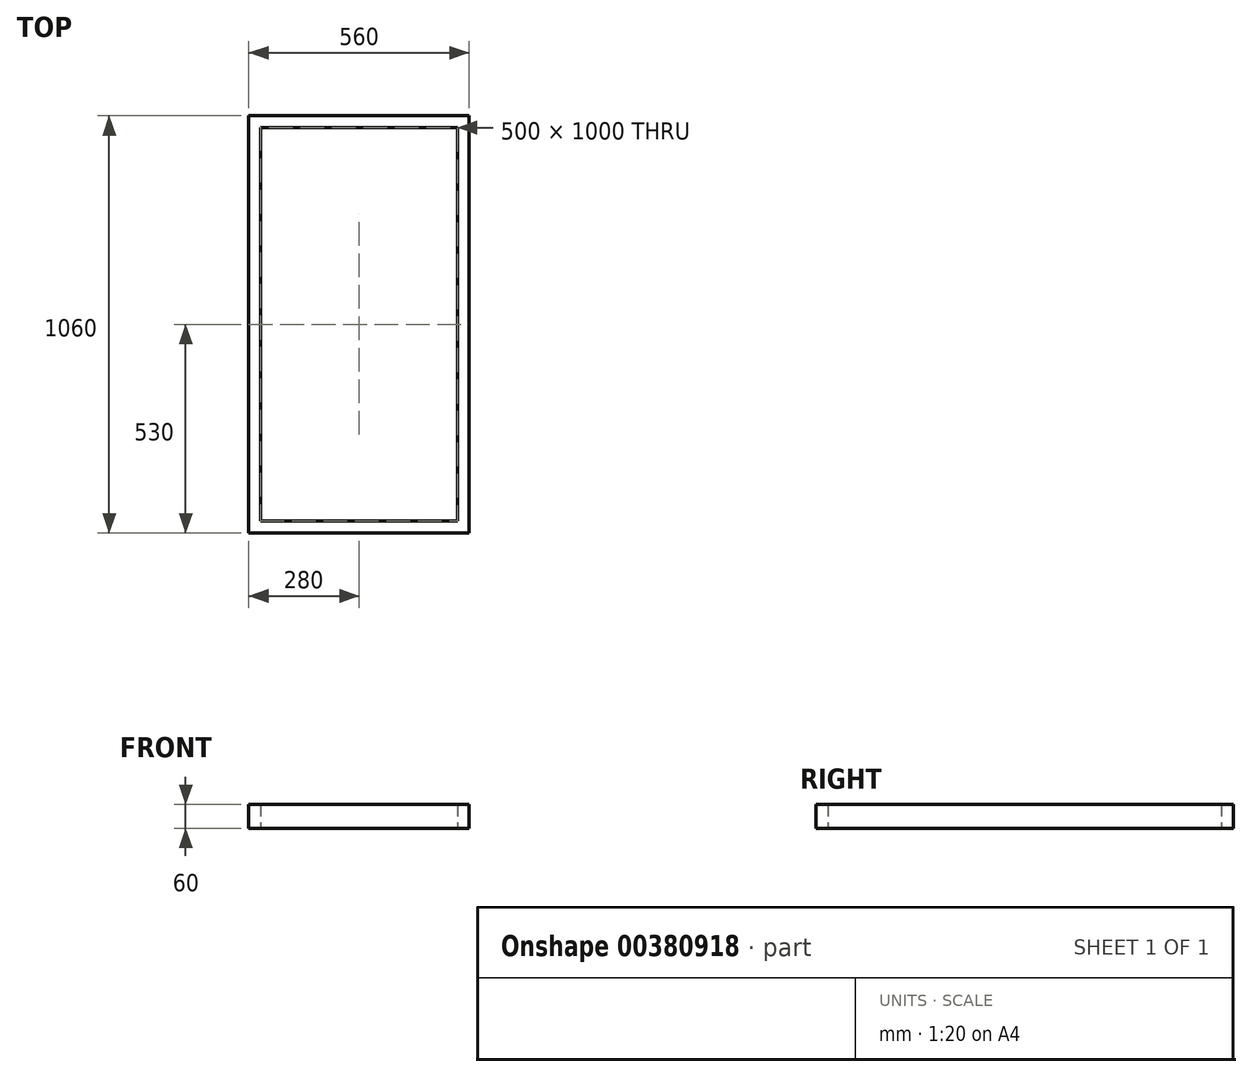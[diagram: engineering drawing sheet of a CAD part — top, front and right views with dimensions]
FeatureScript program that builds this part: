
annotation { "Feature Type Name" : "Feature", "Feature Type Description" : "" }
export const myFeature = defineFeature(function(context is Context, id is Id, definition is map)
    precondition{}
    {
        {
            var Q0;
            Q0=qCreatedBy(makeId("Top.planeOp"),FACE);
            var sketch = newSketch(context, id + "F0", { "sketchPlane" : qUnion([Q0])});
            skLineSegment(sketch, "E0.bottom", {"start": v(250, 500) * mm, "end": v(-250, 500) * mm});
            skLineSegment(sketch, "E0.top", {"start": v(250, -500) * mm, "end": v(-250, -500) * mm});
            skLineSegment(sketch, "E0.left", {"start": v(250, 500) * mm, "end": v(250, -500) * mm});
            skLineSegment(sketch, "E0.right", {"start": v(-250, 500) * mm, "end": v(-250, -500) * mm});
            skPoint(sketch, "E0.middle", {"position": v(0, 0) * mm});
            skLineSegment(sketch, "E1.0", {"start": v(-280, 530) * mm, "end": v(-280, -530) * mm});
            skLineSegment(sketch, "E1.1", {"start": v(280, 530) * mm, "end": v(-280, 530) * mm});
            skLineSegment(sketch, "E1.2", {"start": v(280, 530) * mm, "end": v(280, -530) * mm});
            skLineSegment(sketch, "E1.3", {"start": v(280, -530) * mm, "end": v(-280, -530) * mm});
            skSolve(sketch);
        }
        {
            var Q0;
            Q0=makeQuery(id+"F0.imprint","IMPRINT",FACE,{"disambiguationData":[TD([[makeQuery(id+"F0.imprint","IMPRINT",EDGE,{"derivedFrom":sQuery(id+"F0.wireOp",EDGE,"E0.bottom")}),-1.0]])]});
            extrude(context, id + "F1", {"entities" : qUnion([Q0]), "depth" : 60 * mm});
        }
    });
